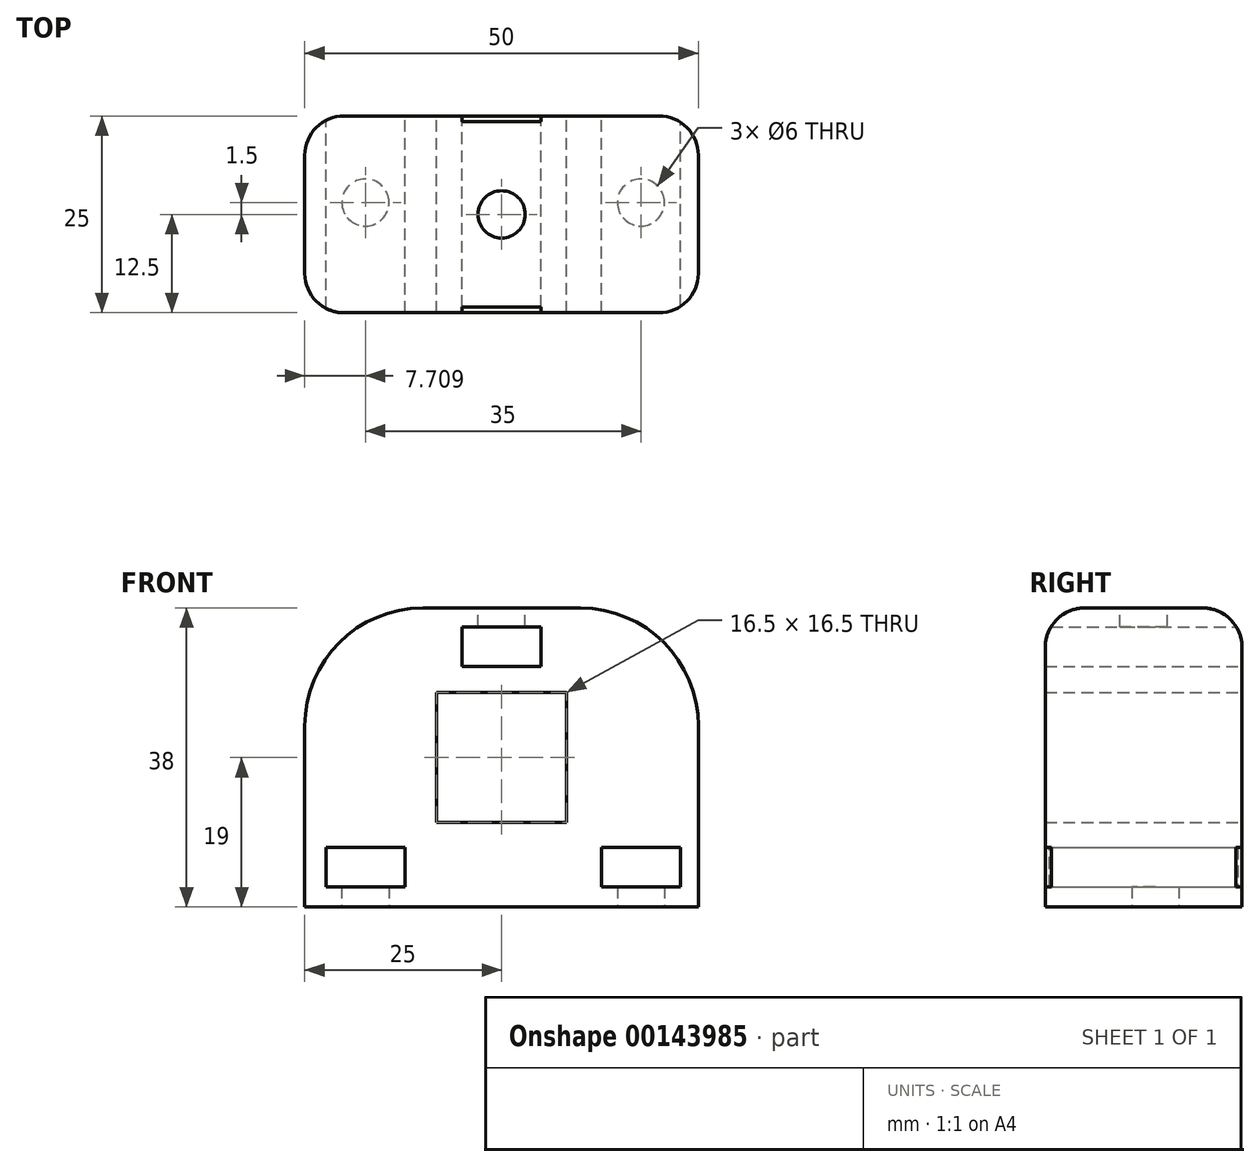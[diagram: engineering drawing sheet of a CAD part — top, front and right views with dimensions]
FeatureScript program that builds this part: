
annotation { "Feature Type Name" : "Feature", "Feature Type Description" : "" }
export const myFeature = defineFeature(function(context is Context, id is Id, definition is map)
    precondition{}
    {
        {
            var Q0;
            Q0=qCreatedBy(makeId("Front.planeOp"),FACE);
            var sketch = newSketch(context, id + "F0", { "sketchPlane" : qUnion([Q0])});
            skLineSegment(sketch, "E0.bottom", {"start": v(-8.25, 8.25) * mm, "end": v(8.25, 8.25) * mm});
            skLineSegment(sketch, "E0.top", {"start": v(-8.25, -8.25) * mm, "end": v(8.25, -8.25) * mm});
            skLineSegment(sketch, "E0.left", {"start": v(-8.25, 8.25) * mm, "end": v(-8.25, -8.25) * mm});
            skLineSegment(sketch, "E0.right", {"start": v(8.25, 8.25) * mm, "end": v(8.25, -8.25) * mm});
            skLineSegment(sketch, "E1.bottom", {"start": v(-25, 19) * mm, "end": v(25, 19) * mm});
            skLineSegment(sketch, "E1.top", {"start": v(-25, -19) * mm, "end": v(25, -19) * mm});
            skLineSegment(sketch, "E1.left", {"start": v(-25, 19) * mm, "end": v(-25, -19) * mm});
            skLineSegment(sketch, "E1.right", {"start": v(25, 19) * mm, "end": v(25, -19) * mm});
            skLineSegment(sketch, "E2.bottom", {"start": v(-5, 16.59) * mm, "end": v(5, 16.59) * mm});
            skLineSegment(sketch, "E2.top", {"start": v(-5, 11.59) * mm, "end": v(5, 11.59) * mm});
            skLineSegment(sketch, "E2.left", {"start": v(-5, 16.59) * mm, "end": v(-5, 11.59) * mm});
            skLineSegment(sketch, "E2.right", {"start": v(5, 16.59) * mm, "end": v(5, 11.59) * mm});
            skLineSegment(sketch, "E3.bottom", {"start": v(12.7, -11.43) * mm, "end": v(22.7, -11.43) * mm});
            skLineSegment(sketch, "E3.top", {"start": v(12.7, -16.43) * mm, "end": v(22.7, -16.43) * mm});
            skLineSegment(sketch, "E3.left", {"start": v(12.7, -11.43) * mm, "end": v(12.7, -16.43) * mm});
            skLineSegment(sketch, "E3.right", {"start": v(22.7, -11.43) * mm, "end": v(22.7, -16.43) * mm});
            skLineSegment(sketch, "E4.bottom", {"start": v(-22.3, -11.43) * mm, "end": v(-12.3, -11.43) * mm});
            skLineSegment(sketch, "E4.top", {"start": v(-22.3, -16.43) * mm, "end": v(-12.3, -16.43) * mm});
            skLineSegment(sketch, "E4.left", {"start": v(-22.3, -11.43) * mm, "end": v(-22.3, -16.43) * mm});
            skLineSegment(sketch, "E4.right", {"start": v(-12.3, -11.43) * mm, "end": v(-12.3, -16.43) * mm});
            skSolve(sketch);
        }
        {
            var Q0;
            Q0=makeQuery(id+"F0.imprint","IMPRINT",FACE,{"disambiguationData":[TD([[makeQuery(id+"F0.imprint","IMPRINT",EDGE,{"derivedFrom":sQuery(id+"F0.wireOp",EDGE,"E0.bottom")}),1.0]])]});
            extrude(context, id + "F1", {"entities" : qUnion([Q0]), "depth" : 25 * mm});
        }
        {
            var Q0;
            Q0=makeQuery(id+"F1.opExtrude","SWEPT_FACE",FACE,{"disambiguationData":[OSD([sQuery(id+"F0.wireOp",EDGE,"E1.bottom")])]});
            var sketch = newSketch(context, id + "F2", { "sketchPlane" : qUnion([Q0])});
            skCircle(sketch, "E5", {"center": v(0, -12.5) * mm, "radius": 3 * mm});
            skPoint(sketch, "E5.centerSnap0", {"position": v(25, -12.5) * mm});
            skSolve(sketch);
        }
        {
            var Q0;
            Q0=makeQuery(id+"F2.imprint","IMPRINT",FACE,{"disambiguationData":[TD([[makeQuery(id+"F2.imprint","IMPRINT",EDGE,{"derivedFrom":sQuery(id+"F2.wireOp",EDGE,"E5")}),1.0]])]});
            var Q1;
            Q1=makeQuery(id+"F1.opExtrude","SWEPT_FACE",FACE,{"disambiguationData":[OSD([sQuery(id+"F0.wireOp",EDGE,"E2.top")])]});
            extrude(context, id + "F3", {"entities" : qUnion([Q0]), "operationType" : NewBodyOperationType.REMOVE, "endBound" : BoundingType.UP_TO_SURFACE, "oppositeDirection" : true, "endBoundEntityFace" : qUnion([Q1]), "depth" : 25 * mm});
        }
        {
            var Q0;
            Q0=makeQuery(id+"F1.opExtrude","SWEPT_FACE",FACE,{"disambiguationData":[OSD([sQuery(id+"F0.wireOp",EDGE,"E1.top")])]});
            var sketch = newSketch(context, id + "F4", { "sketchPlane" : qUnion([Q0])});
            skLineSegment(sketch, "E6.0", {"start": v(-22.3, 25) * mm, "end": v(-22.3, 0) * mm});
            skLineSegment(sketch, "E7.0", {"start": v(22.7, 25) * mm, "end": v(22.7, 0) * mm});
            skLineSegment(sketch, "E8.0", {"start": v(12.7, 25) * mm, "end": v(12.7, 0) * mm});
            skLineSegment(sketch, "E9.0", {"start": v(-12.3, 25) * mm, "end": v(-12.3, 0) * mm});
            skLineSegment(sketch, "E10", {"start": v(-25, 11) * mm, "end": v(25, 11) * mm, "construction": true});
            skCircle(sketch, "E11", {"center": v(17.7, 11) * mm, "radius": 3 * mm});
            skCircle(sketch, "E12", {"center": v(-17.3, 11) * mm, "radius": 3 * mm});
            skSolve(sketch);
        }
        {
            var Q0;
            Q0=makeQuery(id+"F4.imprint","IMPRINT",FACE,{"disambiguationData":[TD([[makeQuery(id+"F4.imprint","IMPRINT",EDGE,{"derivedFrom":sQuery(id+"F4.wireOp",EDGE,"E12")}),1.0]])]});
            var Q1;
            Q1=makeQuery(id+"F4.imprint","IMPRINT",FACE,{"disambiguationData":[TD([[makeQuery(id+"F4.imprint","IMPRINT",EDGE,{"derivedFrom":sQuery(id+"F4.wireOp",EDGE,"E11")}),1.0]])]});
            var Q2;
            Q2=makeQuery(id+"F1.opExtrude","SWEPT_FACE",FACE,{"disambiguationData":[OSD([sQuery(id+"F0.wireOp",EDGE,"E4.bottom")])]});
            extrude(context, id + "F5", {"entities" : qUnion([Q0, Q1]), "operationType" : NewBodyOperationType.REMOVE, "endBound" : BoundingType.UP_TO_SURFACE, "oppositeDirection" : true, "endBoundEntityFace" : qUnion([Q2]), "depth" : 25 * mm});
        }
        {
            var Q0;
            Q0=makeQuery(id+"F1.opExtrude","SWEPT_EDGE",EDGE,{"disambiguationData":[OSD([sQuery(id+"F0.wireOp",EDGE,"E1.bottom"),sQuery(id+"F0.wireOp",EDGE,"E1.left")])]});
            var Q1;
            Q1=makeQuery(id+"F1.opExtrude","SWEPT_EDGE",EDGE,{"disambiguationData":[OSD([sQuery(id+"F0.wireOp",EDGE,"E1.bottom"),sQuery(id+"F0.wireOp",EDGE,"E1.right")])]});
            fillet(context, id + "F6", {"entities" : qUnion([Q0, Q1]), "radius" : 15 * mm, "tangentPropagation" : true, "allowEdgeOverflow" : false});
        }
        {
            var Q0;
            {var subQ0=sQuery(id+"F0.wireOp",EDGE,"E1.left");var subQ1=sQuery(id+"F0.wireOp",EDGE,"E1.bottom");Q0=makeQuery(id+"F6.opFillet","BLEND_EDGE",EDGE,{"blendedFrom":[makeQuery(id+"F1.opExtrude","SWEPT_EDGE",EDGE,{"disambiguationData":[OSD([subQ1,subQ0])]}),makeQuery(id+"F1.opExtrude","CAP_FACE",FACE,{"disambiguationData":[OSD([sQuery(id+"F0.wireOp",EDGE,"E0.bottom"),sQuery(id+"F0.wireOp",EDGE,"E0.top"),sQuery(id+"F0.wireOp",EDGE,"E0.left"),sQuery(id+"F0.wireOp",EDGE,"E0.right"),subQ1,sQuery(id+"F0.wireOp",EDGE,"E1.top"),subQ0,sQuery(id+"F0.wireOp",EDGE,"E1.right"),sQuery(id+"F0.wireOp",EDGE,"E2.bottom"),sQuery(id+"F0.wireOp",EDGE,"E2.top"),sQuery(id+"F0.wireOp",EDGE,"E2.left"),sQuery(id+"F0.wireOp",EDGE,"E2.right"),sQuery(id+"F0.wireOp",EDGE,"E3.bottom"),sQuery(id+"F0.wireOp",EDGE,"E3.top"),sQuery(id+"F0.wireOp",EDGE,"E3.left"),sQuery(id+"F0.wireOp",EDGE,"E3.right"),sQuery(id+"F0.wireOp",EDGE,"E4.bottom"),sQuery(id+"F0.wireOp",EDGE,"E4.top"),sQuery(id+"F0.wireOp",EDGE,"E4.left"),sQuery(id+"F0.wireOp",EDGE,"E4.right")])],"isStart":true})],"blendedInto":[makeQuery(id+"F1.opExtrude","CAP_FACE",FACE,{"disambiguationData":[OSD([sQuery(id+"F0.wireOp",EDGE,"E0.bottom"),sQuery(id+"F0.wireOp",EDGE,"E0.top"),sQuery(id+"F0.wireOp",EDGE,"E0.left"),sQuery(id+"F0.wireOp",EDGE,"E0.right"),subQ1,sQuery(id+"F0.wireOp",EDGE,"E1.top"),subQ0,sQuery(id+"F0.wireOp",EDGE,"E1.right"),sQuery(id+"F0.wireOp",EDGE,"E2.bottom"),sQuery(id+"F0.wireOp",EDGE,"E2.top"),sQuery(id+"F0.wireOp",EDGE,"E2.left"),sQuery(id+"F0.wireOp",EDGE,"E2.right"),sQuery(id+"F0.wireOp",EDGE,"E3.bottom"),sQuery(id+"F0.wireOp",EDGE,"E3.top"),sQuery(id+"F0.wireOp",EDGE,"E3.left"),sQuery(id+"F0.wireOp",EDGE,"E3.right"),sQuery(id+"F0.wireOp",EDGE,"E4.bottom"),sQuery(id+"F0.wireOp",EDGE,"E4.top"),sQuery(id+"F0.wireOp",EDGE,"E4.left"),sQuery(id+"F0.wireOp",EDGE,"E4.right")])],"isStart":true})]});}
            var Q1;
            Q1=makeQuery(id+"F1.opExtrude","CAP_EDGE",EDGE,{"disambiguationData":[OSD([sQuery(id+"F0.wireOp",EDGE,"E1.left")])],"isStart":true});
            var Q2;
            {var subQ0=sQuery(id+"F0.wireOp",EDGE,"E1.right");var subQ1=sQuery(id+"F0.wireOp",EDGE,"E1.bottom");Q2=makeQuery(id+"F6.opFillet","BLEND_EDGE",EDGE,{"blendedFrom":[makeQuery(id+"F1.opExtrude","SWEPT_EDGE",EDGE,{"disambiguationData":[OSD([subQ1,subQ0])]}),makeQuery(id+"F1.opExtrude","CAP_FACE",FACE,{"disambiguationData":[OSD([sQuery(id+"F0.wireOp",EDGE,"E0.bottom"),sQuery(id+"F0.wireOp",EDGE,"E0.top"),sQuery(id+"F0.wireOp",EDGE,"E0.left"),sQuery(id+"F0.wireOp",EDGE,"E0.right"),subQ1,sQuery(id+"F0.wireOp",EDGE,"E1.top"),sQuery(id+"F0.wireOp",EDGE,"E1.left"),subQ0,sQuery(id+"F0.wireOp",EDGE,"E2.bottom"),sQuery(id+"F0.wireOp",EDGE,"E2.top"),sQuery(id+"F0.wireOp",EDGE,"E2.left"),sQuery(id+"F0.wireOp",EDGE,"E2.right"),sQuery(id+"F0.wireOp",EDGE,"E3.bottom"),sQuery(id+"F0.wireOp",EDGE,"E3.top"),sQuery(id+"F0.wireOp",EDGE,"E3.left"),sQuery(id+"F0.wireOp",EDGE,"E3.right"),sQuery(id+"F0.wireOp",EDGE,"E4.bottom"),sQuery(id+"F0.wireOp",EDGE,"E4.top"),sQuery(id+"F0.wireOp",EDGE,"E4.left"),sQuery(id+"F0.wireOp",EDGE,"E4.right")])],"isStart":true})],"blendedInto":[makeQuery(id+"F1.opExtrude","CAP_FACE",FACE,{"disambiguationData":[OSD([sQuery(id+"F0.wireOp",EDGE,"E0.bottom"),sQuery(id+"F0.wireOp",EDGE,"E0.top"),sQuery(id+"F0.wireOp",EDGE,"E0.left"),sQuery(id+"F0.wireOp",EDGE,"E0.right"),subQ1,sQuery(id+"F0.wireOp",EDGE,"E1.top"),sQuery(id+"F0.wireOp",EDGE,"E1.left"),subQ0,sQuery(id+"F0.wireOp",EDGE,"E2.bottom"),sQuery(id+"F0.wireOp",EDGE,"E2.top"),sQuery(id+"F0.wireOp",EDGE,"E2.left"),sQuery(id+"F0.wireOp",EDGE,"E2.right"),sQuery(id+"F0.wireOp",EDGE,"E3.bottom"),sQuery(id+"F0.wireOp",EDGE,"E3.top"),sQuery(id+"F0.wireOp",EDGE,"E3.left"),sQuery(id+"F0.wireOp",EDGE,"E3.right"),sQuery(id+"F0.wireOp",EDGE,"E4.bottom"),sQuery(id+"F0.wireOp",EDGE,"E4.top"),sQuery(id+"F0.wireOp",EDGE,"E4.left"),sQuery(id+"F0.wireOp",EDGE,"E4.right")])],"isStart":true})]});}
            var Q3;
            Q3=makeQuery(id+"F1.opExtrude","CAP_EDGE",EDGE,{"disambiguationData":[OSD([sQuery(id+"F0.wireOp",EDGE,"E1.right")])],"isStart":true});
            var Q4;
            {var subQ0=sQuery(id+"F0.wireOp",EDGE,"E1.right");var subQ1=sQuery(id+"F0.wireOp",EDGE,"E1.bottom");Q4=makeQuery(id+"F6.opFillet","BLEND_EDGE",EDGE,{"blendedFrom":[makeQuery(id+"F1.opExtrude","SWEPT_EDGE",EDGE,{"disambiguationData":[OSD([subQ1,subQ0])]}),makeQuery(id+"F1.opExtrude","CAP_FACE",FACE,{"disambiguationData":[OSD([sQuery(id+"F0.wireOp",EDGE,"E0.bottom"),sQuery(id+"F0.wireOp",EDGE,"E0.top"),sQuery(id+"F0.wireOp",EDGE,"E0.left"),sQuery(id+"F0.wireOp",EDGE,"E0.right"),subQ1,sQuery(id+"F0.wireOp",EDGE,"E1.top"),sQuery(id+"F0.wireOp",EDGE,"E1.left"),subQ0,sQuery(id+"F0.wireOp",EDGE,"E2.bottom"),sQuery(id+"F0.wireOp",EDGE,"E2.top"),sQuery(id+"F0.wireOp",EDGE,"E2.left"),sQuery(id+"F0.wireOp",EDGE,"E2.right"),sQuery(id+"F0.wireOp",EDGE,"E3.bottom"),sQuery(id+"F0.wireOp",EDGE,"E3.top"),sQuery(id+"F0.wireOp",EDGE,"E3.left"),sQuery(id+"F0.wireOp",EDGE,"E3.right"),sQuery(id+"F0.wireOp",EDGE,"E4.bottom"),sQuery(id+"F0.wireOp",EDGE,"E4.top"),sQuery(id+"F0.wireOp",EDGE,"E4.left"),sQuery(id+"F0.wireOp",EDGE,"E4.right")])],"isStart":false})],"blendedInto":[makeQuery(id+"F1.opExtrude","CAP_FACE",FACE,{"disambiguationData":[OSD([sQuery(id+"F0.wireOp",EDGE,"E0.bottom"),sQuery(id+"F0.wireOp",EDGE,"E0.top"),sQuery(id+"F0.wireOp",EDGE,"E0.left"),sQuery(id+"F0.wireOp",EDGE,"E0.right"),subQ1,sQuery(id+"F0.wireOp",EDGE,"E1.top"),sQuery(id+"F0.wireOp",EDGE,"E1.left"),subQ0,sQuery(id+"F0.wireOp",EDGE,"E2.bottom"),sQuery(id+"F0.wireOp",EDGE,"E2.top"),sQuery(id+"F0.wireOp",EDGE,"E2.left"),sQuery(id+"F0.wireOp",EDGE,"E2.right"),sQuery(id+"F0.wireOp",EDGE,"E3.bottom"),sQuery(id+"F0.wireOp",EDGE,"E3.top"),sQuery(id+"F0.wireOp",EDGE,"E3.left"),sQuery(id+"F0.wireOp",EDGE,"E3.right"),sQuery(id+"F0.wireOp",EDGE,"E4.bottom"),sQuery(id+"F0.wireOp",EDGE,"E4.top"),sQuery(id+"F0.wireOp",EDGE,"E4.left"),sQuery(id+"F0.wireOp",EDGE,"E4.right")])],"isStart":false})]});}
            var Q5;
            Q5=makeQuery(id+"F1.opExtrude","CAP_EDGE",EDGE,{"disambiguationData":[OSD([sQuery(id+"F0.wireOp",EDGE,"E1.bottom")])],"isStart":false});
            var Q6;
            {var subQ0=sQuery(id+"F0.wireOp",EDGE,"E1.left");var subQ1=sQuery(id+"F0.wireOp",EDGE,"E1.bottom");Q6=makeQuery(id+"F6.opFillet","BLEND_EDGE",EDGE,{"blendedFrom":[makeQuery(id+"F1.opExtrude","SWEPT_EDGE",EDGE,{"disambiguationData":[OSD([subQ1,subQ0])]}),makeQuery(id+"F1.opExtrude","CAP_FACE",FACE,{"disambiguationData":[OSD([sQuery(id+"F0.wireOp",EDGE,"E0.bottom"),sQuery(id+"F0.wireOp",EDGE,"E0.top"),sQuery(id+"F0.wireOp",EDGE,"E0.left"),sQuery(id+"F0.wireOp",EDGE,"E0.right"),subQ1,sQuery(id+"F0.wireOp",EDGE,"E1.top"),subQ0,sQuery(id+"F0.wireOp",EDGE,"E1.right"),sQuery(id+"F0.wireOp",EDGE,"E2.bottom"),sQuery(id+"F0.wireOp",EDGE,"E2.top"),sQuery(id+"F0.wireOp",EDGE,"E2.left"),sQuery(id+"F0.wireOp",EDGE,"E2.right"),sQuery(id+"F0.wireOp",EDGE,"E3.bottom"),sQuery(id+"F0.wireOp",EDGE,"E3.top"),sQuery(id+"F0.wireOp",EDGE,"E3.left"),sQuery(id+"F0.wireOp",EDGE,"E3.right"),sQuery(id+"F0.wireOp",EDGE,"E4.bottom"),sQuery(id+"F0.wireOp",EDGE,"E4.top"),sQuery(id+"F0.wireOp",EDGE,"E4.left"),sQuery(id+"F0.wireOp",EDGE,"E4.right")])],"isStart":false})],"blendedInto":[makeQuery(id+"F1.opExtrude","CAP_FACE",FACE,{"disambiguationData":[OSD([sQuery(id+"F0.wireOp",EDGE,"E0.bottom"),sQuery(id+"F0.wireOp",EDGE,"E0.top"),sQuery(id+"F0.wireOp",EDGE,"E0.left"),sQuery(id+"F0.wireOp",EDGE,"E0.right"),subQ1,sQuery(id+"F0.wireOp",EDGE,"E1.top"),subQ0,sQuery(id+"F0.wireOp",EDGE,"E1.right"),sQuery(id+"F0.wireOp",EDGE,"E2.bottom"),sQuery(id+"F0.wireOp",EDGE,"E2.top"),sQuery(id+"F0.wireOp",EDGE,"E2.left"),sQuery(id+"F0.wireOp",EDGE,"E2.right"),sQuery(id+"F0.wireOp",EDGE,"E3.bottom"),sQuery(id+"F0.wireOp",EDGE,"E3.top"),sQuery(id+"F0.wireOp",EDGE,"E3.left"),sQuery(id+"F0.wireOp",EDGE,"E3.right"),sQuery(id+"F0.wireOp",EDGE,"E4.bottom"),sQuery(id+"F0.wireOp",EDGE,"E4.top"),sQuery(id+"F0.wireOp",EDGE,"E4.left"),sQuery(id+"F0.wireOp",EDGE,"E4.right")])],"isStart":false})]});}
            var Q7;
            Q7=makeQuery(id+"F1.opExtrude","CAP_EDGE",EDGE,{"disambiguationData":[OSD([sQuery(id+"F0.wireOp",EDGE,"E1.bottom")])],"isStart":true});
            var Q8;
            Q8=makeQuery(id+"F1.opExtrude","CAP_EDGE",EDGE,{"disambiguationData":[OSD([sQuery(id+"F0.wireOp",EDGE,"E1.right")])],"isStart":false});
            var Q9;
            Q9=makeQuery(id+"F1.opExtrude","CAP_EDGE",EDGE,{"disambiguationData":[OSD([sQuery(id+"F0.wireOp",EDGE,"E1.left")])],"isStart":false});
            fillet(context, id + "F7", {"entities" : qUnion([Q0, Q1, Q2, Q3, Q4, Q5, Q6, Q7, Q8, Q9]), "radius" : 5 * mm, "tangentPropagation" : true, "allowEdgeOverflow" : false});
        }
    });
